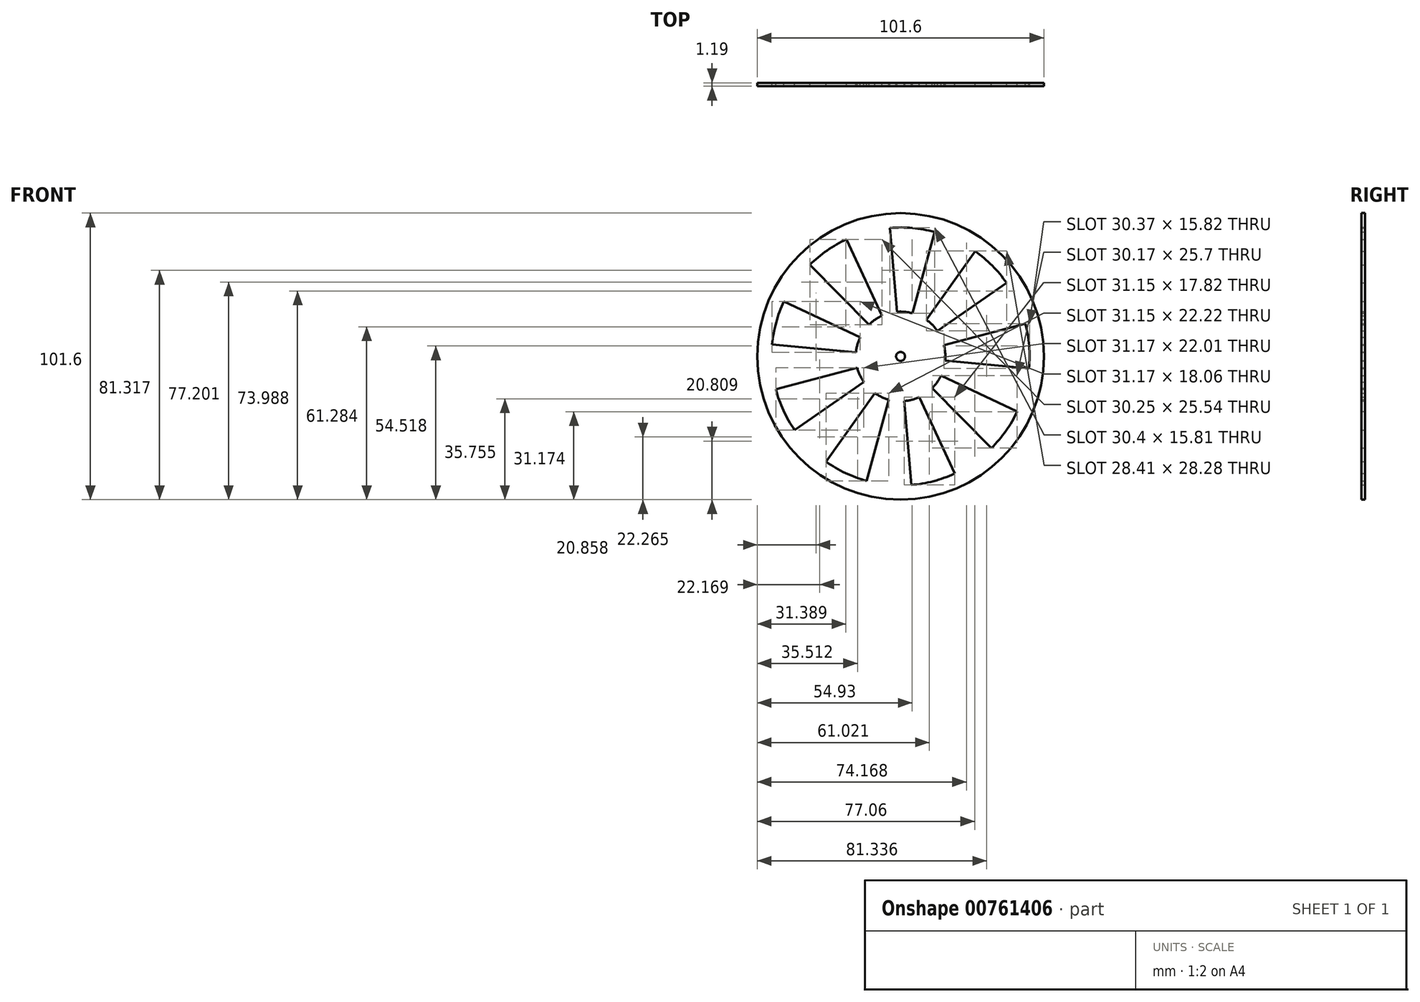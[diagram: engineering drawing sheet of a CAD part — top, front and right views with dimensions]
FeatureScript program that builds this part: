
annotation { "Feature Type Name" : "Feature", "Feature Type Description" : "" }
export const myFeature = defineFeature(function(context is Context, id is Id, definition is map)
    precondition{}
    {
        {
            var Q0;
            Q0=qCreatedBy(makeId("Front.planeOp"),FACE);
            var sketch = newSketch(context, id + "F0", { "sketchPlane" : qUnion([Q0])});
            skCircle(sketch, "E0", {"center": v(0, 0) * mm, "radius": 50.8 * mm});
            skCircle(sketch, "E1", {"center": v(0, 0) * mm, "radius": 45.72 * mm});
            skCircle(sketch, "E2", {"center": v(0, 0) * mm, "radius": 15.88 * mm});
            skLineSegment(sketch, "E3", {"start": v(-6.64, 14.42) * mm, "end": v(-19.13, 41.52) * mm});
            skLineSegment(sketch, "E4", {"start": v(-1.31, 15.82) * mm, "end": v(-3.78, 45.56) * mm});
            skLineSegment(sketch, "E5", {"start": v(12.04, 44.1) * mm, "end": v(4.18, 15.32) * mm});
            skLineSegment(sketch, "E6", {"start": v(9.17, 12.96) * mm, "end": v(26.4, 37.33) * mm});
            skLineSegment(sketch, "E7", {"start": v(13.05, 9.05) * mm, "end": v(37.57, 26.05) * mm});
            skLineSegment(sketch, "E8", {"start": v(15.35, 4.04) * mm, "end": v(44.22, 11.63) * mm});
            skLineSegment(sketch, "E9", {"start": v(15.8, -1.46) * mm, "end": v(45.53, -4.2) * mm});
            skLineSegment(sketch, "E10", {"start": v(-15.35, -4.04) * mm, "end": v(-44.22, -11.63) * mm});
            skLineSegment(sketch, "E11", {"start": v(-15.8, 1.46) * mm, "end": v(-45.53, 4.2) * mm});
            skLineSegment(sketch, "E12", {"start": v(-11.17, 11.28) * mm, "end": v(-32.18, 32.48) * mm});
            skLineSegment(sketch, "E13", {"start": v(11.17, -11.28) * mm, "end": v(32.18, -32.48) * mm});
            skLineSegment(sketch, "E14", {"start": v(14.36, -6.78) * mm, "end": v(41.35, -19.51) * mm});
            skLineSegment(sketch, "E15", {"start": v(-41.35, 19.51) * mm, "end": v(-14.36, 6.78) * mm});
            skLineSegment(sketch, "E16", {"start": v(-13.05, -9.05) * mm, "end": v(-37.57, -26.05) * mm});
            skLineSegment(sketch, "E17", {"start": v(-9.17, -12.96) * mm, "end": v(-26.4, -37.33) * mm});
            skLineSegment(sketch, "E18", {"start": v(-4.18, -15.32) * mm, "end": v(-12.04, -44.1) * mm});
            skLineSegment(sketch, "E19", {"start": v(1.31, -15.82) * mm, "end": v(3.78, -45.56) * mm});
            skLineSegment(sketch, "E20", {"start": v(6.64, -14.42) * mm, "end": v(19.13, -41.52) * mm});
            skCircle(sketch, "E21", {"center": v(0, 0) * mm, "radius": 1.59 * mm});
            skSolve(sketch);
        }
        {
            var Q0;
            Q0 = qSketchRegion(id + "F0", true);
            var Q1;
            {var subQ0=sQuery(id+"F0.wireOp",EDGE,"E10");Q1=makeQuery(id+"F0.imprint","IMPRINT",FACE,{"disambiguationData":[TD([[makeQuery(id+"F0.imprint","IMPRINT",EDGE,{"derivedFrom":subQ0}),-1.0]])]});}
            var Q2;
            {var subQ0=sQuery(id+"F0.wireOp",EDGE,"E12");Q2=makeQuery(id+"F0.imprint","IMPRINT",FACE,{"disambiguationData":[TD([[makeQuery(id+"F0.imprint","IMPRINT",EDGE,{"derivedFrom":subQ0}),1.0]])]});}
            var Q3;
            {var subQ0=sQuery(id+"F0.wireOp",EDGE,"E3");Q3=makeQuery(id+"F0.imprint","IMPRINT",FACE,{"disambiguationData":[TD([[makeQuery(id+"F0.imprint","IMPRINT",EDGE,{"derivedFrom":subQ0}),-1.0]])]});}
            var Q4;
            {var subQ0=sQuery(id+"F0.wireOp",EDGE,"E5");Q4=makeQuery(id+"F0.imprint","IMPRINT",FACE,{"disambiguationData":[TD([[makeQuery(id+"F0.imprint","IMPRINT",EDGE,{"derivedFrom":subQ0}),1.0]])]});}
            var Q5;
            {var subQ0=sQuery(id+"F0.wireOp",EDGE,"E7");Q5=makeQuery(id+"F0.imprint","IMPRINT",FACE,{"disambiguationData":[TD([[makeQuery(id+"F0.imprint","IMPRINT",EDGE,{"derivedFrom":subQ0}),-1.0]])]});}
            var Q6;
            {var subQ0=sQuery(id+"F0.wireOp",EDGE,"E9");Q6=makeQuery(id+"F0.imprint","IMPRINT",FACE,{"disambiguationData":[TD([[makeQuery(id+"F0.imprint","IMPRINT",EDGE,{"derivedFrom":subQ0}),-1.0]])]});}
            var Q7;
            {var subQ0=sQuery(id+"F0.wireOp",EDGE,"E13");Q7=makeQuery(id+"F0.imprint","IMPRINT",FACE,{"disambiguationData":[TD([[makeQuery(id+"F0.imprint","IMPRINT",EDGE,{"derivedFrom":subQ0}),-1.0]])]});}
            var Q8;
            {var subQ0=sQuery(id+"F0.wireOp",EDGE,"E18");Q8=makeQuery(id+"F0.imprint","IMPRINT",FACE,{"disambiguationData":[TD([[makeQuery(id+"F0.imprint","IMPRINT",EDGE,{"derivedFrom":subQ0}),1.0]])]});}
            var Q9;
            {var subQ0=sQuery(id+"F0.wireOp",EDGE,"E16");Q9=makeQuery(id+"F0.imprint","IMPRINT",FACE,{"disambiguationData":[TD([[makeQuery(id+"F0.imprint","IMPRINT",EDGE,{"derivedFrom":subQ0}),1.0]])]});}
            var Q10;
            {var subQ0=sQuery(id+"F0.wireOp",EDGE,"E2");var subQ8=makeQuery(id+"F0.imprint","INTERSECT",VERTEX,{"derivedFrom":[subQ0,sQuery(id+"F0.wireOp",EDGE,"E7")]});Q10=makeQuery(id+"F0.imprint","IMPRINT",FACE,{"disambiguationData":[TD([[makeQuery(id+"F0.imprint","IMPRINT",EDGE,{"disambiguationData":[TD([[subQ8,1.0]])],"derivedFrom":subQ0}),1.0]])]});}
            extrude(context, id + "F1", {"entities" : qUnion([Q0, Q1, Q2, Q3, Q4, Q5, Q6, Q7, Q8, Q9, Q10]), "depth" : 1.2 * mm, "offsetDistance" : 25.4 * mm});
        }
    });
